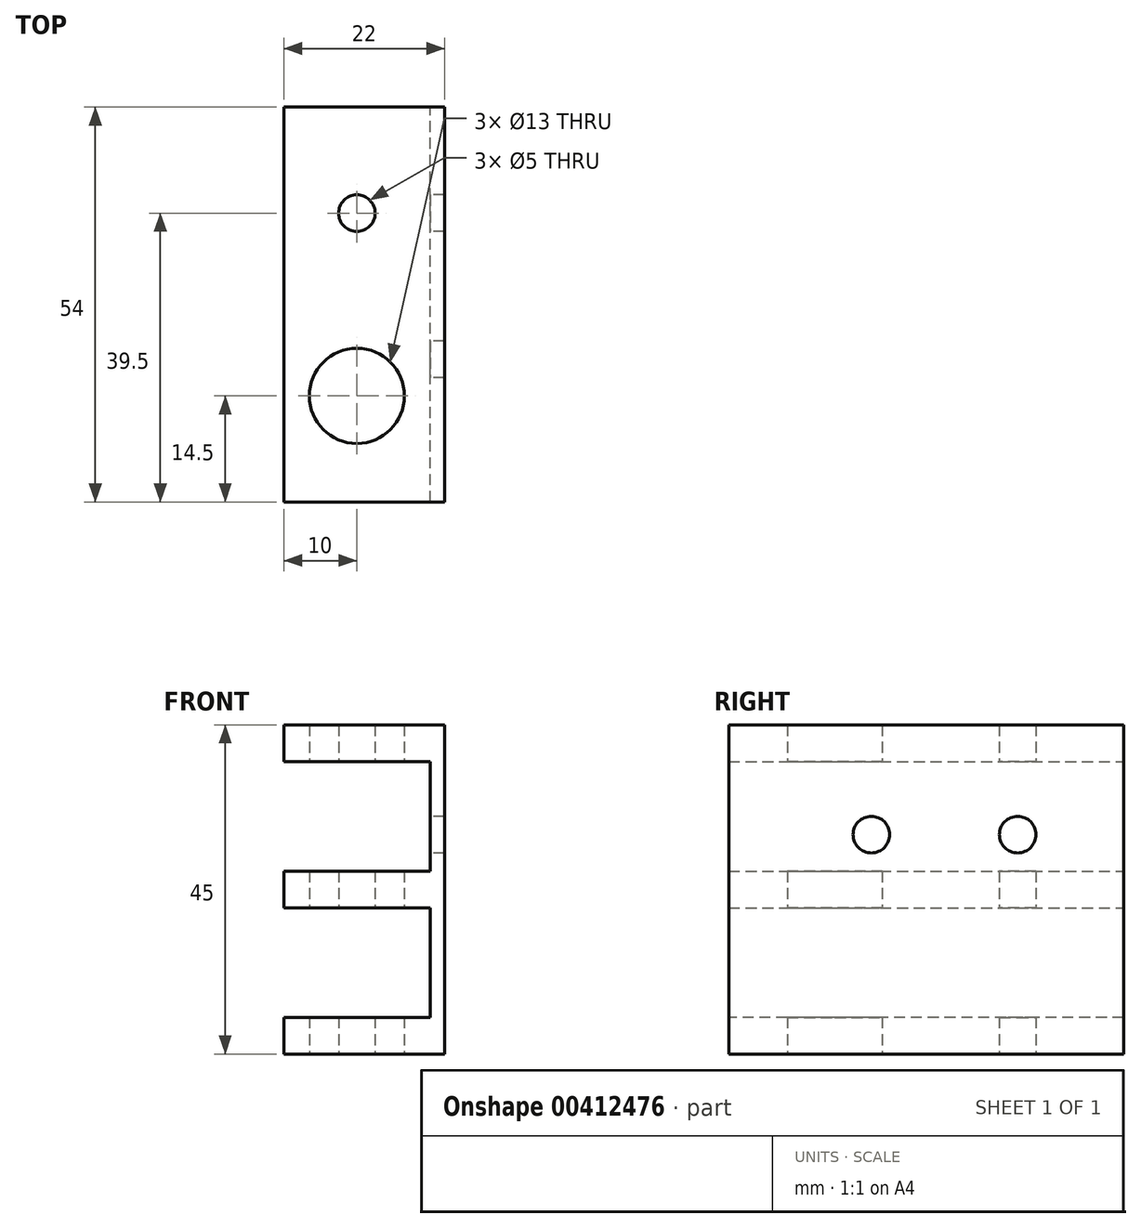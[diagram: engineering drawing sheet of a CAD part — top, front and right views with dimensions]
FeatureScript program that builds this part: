
annotation { "Feature Type Name" : "Feature", "Feature Type Description" : "" }
export const myFeature = defineFeature(function(context is Context, id is Id, definition is map)
    precondition{}
    {
        {
            var Q0;
            Q0=qCreatedBy(makeId("Top.planeOp"),FACE);
            var sketch = newSketch(context, id + "F0", { "sketchPlane" : qUnion([Q0])});
            skLineSegment(sketch, "E0.bottom", {"start": v(10, 12.5) * mm, "end": v(-10, 12.5) * mm});
            skLineSegment(sketch, "E0.top", {"start": v(10, -12.5) * mm, "end": v(-10, -12.5) * mm});
            skLineSegment(sketch, "E0.left", {"start": v(10, 12.5) * mm, "end": v(10, -12.5) * mm});
            skLineSegment(sketch, "E0.right", {"start": v(-10, 12.5) * mm, "end": v(-10, -12.5) * mm});
            skPoint(sketch, "E0.middle", {"position": v(0, 0) * mm});
            skCircle(sketch, "E1", {"center": v(0, 0) * mm, "radius": 2.5 * mm});
            skCircle(sketch, "E2.0", {"center": v(0, 0) * mm, "radius": 6.5 * mm});
            skLineSegment(sketch, "E3.0", {"start": v(12, 14.5) * mm, "end": v(-10, 14.5) * mm});
            skLineSegment(sketch, "E3.1", {"start": v(12, 14.5) * mm, "end": v(12, -12.5) * mm});
            skLineSegment(sketch, "E4", {"start": v(-10, 14.5) * mm, "end": v(-10, 12.5) * mm});
            skLineSegment(sketch, "E5", {"start": v(12, -12.5) * mm, "end": v(10, -12.5) * mm});
            skLineSegment(sketch, "E6.MirrorCS", {"start": v(-10, -39.5) * mm, "end": v(-10, -37.5) * mm});
            skLineSegment(sketch, "E7.MirrorCS", {"start": v(12, -39.5) * mm, "end": v(12, -12.5) * mm});
            skPoint(sketch, "E8.MirrorP", {"position": v(0, -25) * mm});
            skLineSegment(sketch, "E9.MirrorCS", {"start": v(12, -39.5) * mm, "end": v(-10, -39.5) * mm});
            skCircle(sketch, "E10.MirrorC", {"center": v(0, -25) * mm, "radius": 6.5 * mm});
            skCircle(sketch, "E11.MirrorC", {"center": v(0, -25) * mm, "radius": 2.5 * mm});
            skLineSegment(sketch, "E12.MirrorCS", {"start": v(-10, -37.5) * mm, "end": v(-10, -12.5) * mm});
            skLineSegment(sketch, "E13.MirrorCS", {"start": v(10, -37.5) * mm, "end": v(10, -12.5) * mm});
            skLineSegment(sketch, "E14.MirrorCS", {"start": v(10, -37.5) * mm, "end": v(-10, -37.5) * mm});
            skLineSegment(sketch, "E15", {"start": v(10, -37.5) * mm, "end": v(10, -39.5) * mm});
            skLineSegment(sketch, "E16", {"start": v(10, 12.5) * mm, "end": v(10, 14.5) * mm});
            skSolve(sketch);
        }
        {
            var Q0;
            Q0=makeQuery(id+"F0.imprint","IMPRINT",FACE,{"disambiguationData":[TD([[makeQuery(id+"F0.imprint","IMPRINT",EDGE,{"derivedFrom":sQuery(id+"F0.wireOp",EDGE,"E0.bottom")}),1.0]])]});
            var Q1;
            Q1=makeQuery(id+"F0.imprint","IMPRINT",FACE,{"disambiguationData":[TD([[makeQuery(id+"F0.imprint","IMPRINT",EDGE,{"derivedFrom":sQuery(id+"F0.wireOp",EDGE,"E1")}),-1.0]])]});
            var Q2;
            Q2=makeQuery(id+"F0.imprint","IMPRINT",FACE,{"disambiguationData":[TD([[makeQuery(id+"F0.imprint","IMPRINT",EDGE,{"derivedFrom":sQuery(id+"F0.wireOp",EDGE,"E0.bottom")}),-1.0]])]});
            var Q3;
            Q3=makeQuery(id+"F0.imprint","IMPRINT",FACE,{"disambiguationData":[TD([[makeQuery(id+"F0.imprint","IMPRINT",EDGE,{"derivedFrom":sQuery(id+"F0.wireOp",EDGE,"E0.top")}),1.0]])]});
            var Q4;
            Q4=makeQuery(id+"F0.imprint","IMPRINT",FACE,{"disambiguationData":[TD([[makeQuery(id+"F0.imprint","IMPRINT",EDGE,{"derivedFrom":sQuery(id+"F0.wireOp",EDGE,"E10.MirrorC")}),-1.0]])]});
            var Q5;
            Q5=makeQuery(id+"F0.imprint","IMPRINT",FACE,{"disambiguationData":[TD([[makeQuery(id+"F0.imprint","IMPRINT",EDGE,{"derivedFrom":sQuery(id+"F0.wireOp",EDGE,"E5")}),1.0]])]});
            var Q6;
            {var subQ0=sQuery(id+"F0.wireOp",EDGE,"E6.MirrorCS");Q6=makeQuery(id+"F0.imprint","IMPRINT",FACE,{"disambiguationData":[TD([[makeQuery(id+"F0.imprint","IMPRINT",EDGE,{"derivedFrom":subQ0}),-1.0]])]});}
            var Q7;
            Q7=makeQuery(id+"F0.imprint","IMPRINT",FACE,{"disambiguationData":[TD([[makeQuery(id+"F0.imprint","IMPRINT",EDGE,{"derivedFrom":sQuery(id+"F0.wireOp",EDGE,"E0.left")}),1.0]])]});
            extrude(context, id + "F1", {"entities" : qUnion([Q0, Q1, Q2, Q3, Q4, Q5, Q6, Q7]), "depth" : 5 * mm});
        }
        {
            var Q0;
            Q0=makeQuery(id+"F0.imprint","IMPRINT",FACE,{"disambiguationData":[TD([[makeQuery(id+"F0.imprint","IMPRINT",EDGE,{"derivedFrom":sQuery(id+"F0.wireOp",EDGE,"E5")}),1.0]])]});
            var Q1;
            Q1=makeQuery(id+"F0.imprint","IMPRINT",FACE,{"disambiguationData":[TD([[makeQuery(id+"F0.imprint","IMPRINT",EDGE,{"derivedFrom":sQuery(id+"F0.wireOp",EDGE,"E0.left")}),1.0]])]});
            extrude(context, id + "F2", {"entities" : qUnion([Q0, Q1]), "operationType" : NewBodyOperationType.ADD, "depth" : 45 * mm});
        }
        {
            var Q0;
            Q0=makeQuery(id+"F0.imprint","IMPRINT",FACE,{"disambiguationData":[TD([[makeQuery(id+"F0.imprint","IMPRINT",EDGE,{"derivedFrom":sQuery(id+"F0.wireOp",EDGE,"E0.bottom")}),1.0]])]});
            var Q1;
            Q1=makeQuery(id+"F0.imprint","IMPRINT",FACE,{"disambiguationData":[TD([[makeQuery(id+"F0.imprint","IMPRINT",EDGE,{"derivedFrom":sQuery(id+"F0.wireOp",EDGE,"E1")}),-1.0]])]});
            var Q2;
            Q2=makeQuery(id+"F0.imprint","IMPRINT",FACE,{"disambiguationData":[TD([[makeQuery(id+"F0.imprint","IMPRINT",EDGE,{"derivedFrom":sQuery(id+"F0.wireOp",EDGE,"E0.bottom")}),-1.0]])]});
            var Q3;
            Q3=makeQuery(id+"F0.imprint","IMPRINT",FACE,{"disambiguationData":[TD([[makeQuery(id+"F0.imprint","IMPRINT",EDGE,{"derivedFrom":sQuery(id+"F0.wireOp",EDGE,"E5")}),1.0]])]});
            var Q4;
            Q4=makeQuery(id+"F0.imprint","IMPRINT",FACE,{"disambiguationData":[TD([[makeQuery(id+"F0.imprint","IMPRINT",EDGE,{"derivedFrom":sQuery(id+"F0.wireOp",EDGE,"E0.top")}),1.0]])]});
            var Q5;
            Q5=makeQuery(id+"F0.imprint","IMPRINT",FACE,{"disambiguationData":[TD([[makeQuery(id+"F0.imprint","IMPRINT",EDGE,{"derivedFrom":sQuery(id+"F0.wireOp",EDGE,"E10.MirrorC")}),-1.0]])]});
            var Q6;
            {var subQ0=sQuery(id+"F0.wireOp",EDGE,"E6.MirrorCS");Q6=makeQuery(id+"F0.imprint","IMPRINT",FACE,{"disambiguationData":[TD([[makeQuery(id+"F0.imprint","IMPRINT",EDGE,{"derivedFrom":subQ0}),-1.0]])]});}
            var Q7;
            Q7=makeQuery(id+"F0.imprint","IMPRINT",FACE,{"disambiguationData":[TD([[makeQuery(id+"F0.imprint","IMPRINT",EDGE,{"derivedFrom":sQuery(id+"F0.wireOp",EDGE,"E0.left")}),1.0]])]});
            extrude(context, id + "F3", {"entities" : qUnion([Q0, Q1, Q2, Q3, Q4, Q5, Q6, Q7]), "operationType" : NewBodyOperationType.ADD, "depth" : 25 * mm, "hasSecondDirection" : true, "secondDirectionOppositeDirection" : false, "secondDirectionDepth" : 20 * mm});
        }
        {
            var Q0;
            Q0=makeQuery(id+"F0.imprint","IMPRINT",FACE,{"disambiguationData":[TD([[makeQuery(id+"F0.imprint","IMPRINT",EDGE,{"derivedFrom":sQuery(id+"F0.wireOp",EDGE,"E0.bottom")}),-1.0]])]});
            var Q1;
            Q1=makeQuery(id+"F0.imprint","IMPRINT",FACE,{"disambiguationData":[TD([[makeQuery(id+"F0.imprint","IMPRINT",EDGE,{"derivedFrom":sQuery(id+"F0.wireOp",EDGE,"E0.bottom")}),1.0]])]});
            var Q2;
            Q2=makeQuery(id+"F0.imprint","IMPRINT",FACE,{"disambiguationData":[TD([[makeQuery(id+"F0.imprint","IMPRINT",EDGE,{"derivedFrom":sQuery(id+"F0.wireOp",EDGE,"E1")}),-1.0]])]});
            var Q3;
            Q3=makeQuery(id+"F0.imprint","IMPRINT",FACE,{"disambiguationData":[TD([[makeQuery(id+"F0.imprint","IMPRINT",EDGE,{"derivedFrom":sQuery(id+"F0.wireOp",EDGE,"E0.top")}),1.0]])]});
            var Q4;
            Q4=makeQuery(id+"F0.imprint","IMPRINT",FACE,{"disambiguationData":[TD([[makeQuery(id+"F0.imprint","IMPRINT",EDGE,{"derivedFrom":sQuery(id+"F0.wireOp",EDGE,"E10.MirrorC")}),-1.0]])]});
            var Q5;
            Q5=makeQuery(id+"F0.imprint","IMPRINT",FACE,{"disambiguationData":[TD([[makeQuery(id+"F0.imprint","IMPRINT",EDGE,{"derivedFrom":sQuery(id+"F0.wireOp",EDGE,"E5")}),1.0]])]});
            var Q6;
            {var subQ0=sQuery(id+"F0.wireOp",EDGE,"E6.MirrorCS");Q6=makeQuery(id+"F0.imprint","IMPRINT",FACE,{"disambiguationData":[TD([[makeQuery(id+"F0.imprint","IMPRINT",EDGE,{"derivedFrom":subQ0}),-1.0]])]});}
            var Q7;
            Q7=makeQuery(id+"F0.imprint","IMPRINT",FACE,{"disambiguationData":[TD([[makeQuery(id+"F0.imprint","IMPRINT",EDGE,{"derivedFrom":sQuery(id+"F0.wireOp",EDGE,"E0.left")}),1.0]])]});
            extrude(context, id + "F4", {"entities" : qUnion([Q0, Q1, Q2, Q3, Q4, Q5, Q6, Q7]), "operationType" : NewBodyOperationType.ADD, "depth" : 45 * mm, "hasSecondDirection" : true, "secondDirectionOppositeDirection" : false, "secondDirectionDepth" : 40 * mm});
        }
        {
            var Q0;
            {var subQ0=sQuery(id+"F0.wireOp",EDGE,"E5");var subQ1=sQuery(id+"F0.wireOp",EDGE,"E4");var subQ2=sQuery(id+"F0.wireOp",EDGE,"E3.1");var subQ3=sQuery(id+"F0.wireOp",EDGE,"E3.0");var subQ4=sQuery(id+"F0.wireOp",EDGE,"E0.left");var subQ5=sQuery(id+"F0.wireOp",EDGE,"E0.bottom");Q0=makeQuery(id+"F3.boolean.opBoolean","SPLIT",FACE,{"disambiguationData":[TD([makeQuery(id+"F2.opExtrude","CAP_FACE",FACE,{"disambiguationData":[OSD([subQ5,subQ4,subQ3,subQ2,subQ1,subQ0])],"isStart":false})])],"derivedFrom":makeQuery(id+"F2.opExtrude","SWEPT_FACE",FACE,{"disambiguationData":[OSD([subQ4])]})});}
            var sketch = newSketch(context, id + "F5", { "sketchPlane" : qUnion([Q0])});
            skPoint(sketch, "E17", {"position": v(0, 30) * mm});
            skPoint(sketch, "E18", {"position": v(20, 30) * mm});
            skSolve(sketch);
        }
        {
            var Q0;
            Q0=sQuery(id+"F5.wireOp",VERTEX,"E17");
            var Q1;
            Q1=sQuery(id+"F5.wireOp",VERTEX,"E18");
            var Q2;
            Q2=makeQuery(id+"F1.opExtrude","SWEPT_BODY",BODY,{"disambiguationData":[OSD([sQuery(id+"F0.wireOp",EDGE,"E0.top"),sQuery(id+"F0.wireOp",EDGE,"E0.right"),sQuery(id+"F0.wireOp",EDGE,"E1"),sQuery(id+"F0.wireOp",EDGE,"E3.0"),sQuery(id+"F0.wireOp",EDGE,"E3.1"),sQuery(id+"F0.wireOp",EDGE,"E4"),sQuery(id+"F0.wireOp",EDGE,"E5")])]});
            hole(context, id + "F6", {"style" : HoleStyle.SIMPLE, "endStyle" : HoleEndStyle.BLIND, "holeDiameter" : 5 * mm, "holeDepth" : 12.7 * mm, "isTappedThrough" : true, "tappedDepth" : 12 * mm, "tapClearance" : 3, "locations" : qUnion([Q0, Q1]), "scope" : qUnion([Q2])});
        }
    });
